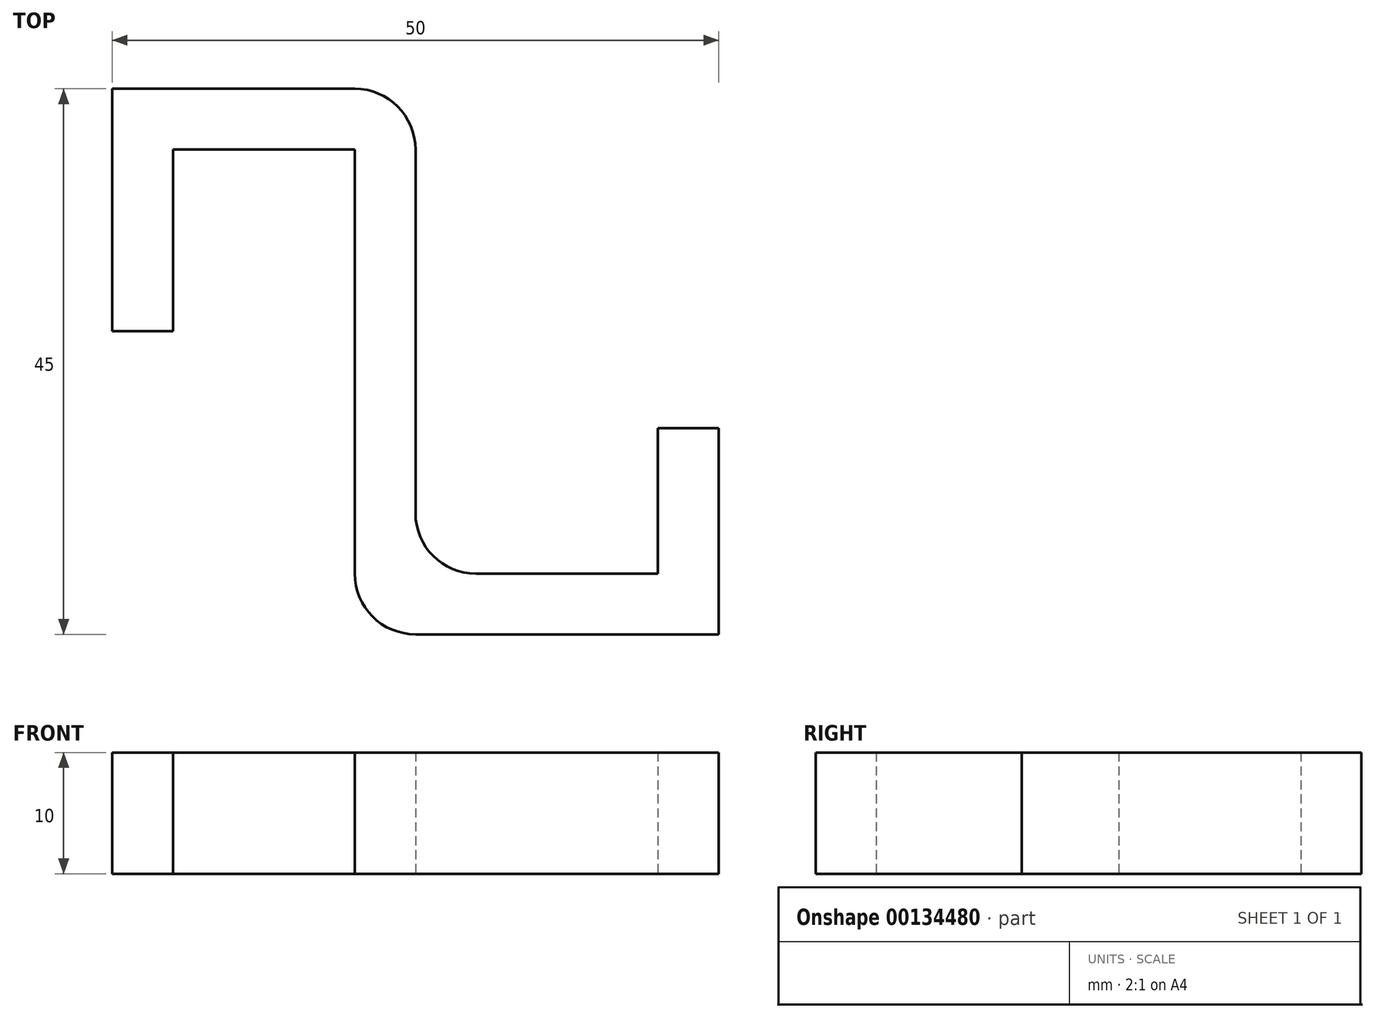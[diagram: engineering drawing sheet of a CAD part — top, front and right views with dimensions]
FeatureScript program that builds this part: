
annotation { "Feature Type Name" : "Feature", "Feature Type Description" : "" }
export const myFeature = defineFeature(function(context is Context, id is Id, definition is map)
    precondition{}
    {
        {
            var Q0;
            Q0=qCreatedBy(makeId("Top.planeOp"),FACE);
            var sketch = newSketch(context, id + "F0", { "sketchPlane" : qUnion([Q0])});
            skLineSegment(sketch, "E0", {"start": v(0, 0) * mm, "end": v(0, 15) * mm});
            skLineSegment(sketch, "E1", {"start": v(0, 15) * mm, "end": v(15, 15) * mm});
            skLineSegment(sketch, "E2", {"start": v(15, 15) * mm, "end": v(15, -25) * mm});
            skLineSegment(sketch, "E3", {"start": v(15, -25) * mm, "end": v(45, -25) * mm});
            skLineSegment(sketch, "E4", {"start": v(45, -25) * mm, "end": v(45, -8) * mm});
            skLineSegment(sketch, "E5", {"start": v(45, -8) * mm, "end": v(40, -8) * mm});
            skLineSegment(sketch, "E6", {"start": v(40, -8) * mm, "end": v(40, -20) * mm});
            skLineSegment(sketch, "E7", {"start": v(40, -20) * mm, "end": v(20, -20) * mm});
            skLineSegment(sketch, "E8", {"start": v(20, -20) * mm, "end": v(20, 20) * mm});
            skLineSegment(sketch, "E9", {"start": v(20, 20) * mm, "end": v(-5, 20) * mm});
            skLineSegment(sketch, "E10", {"start": v(-5, 20) * mm, "end": v(-5, 0) * mm});
            skLineSegment(sketch, "E11", {"start": v(-5, 0) * mm, "end": v(0, 0) * mm});
            skSolve(sketch);
        }
        {
            var Q0;
            Q0 = qSketchRegion(id + "F0", true);
            extrude(context, id + "F1", {"entities" : qUnion([Q0]), "depth" : 10 * mm});
        }
        {
            var Q0;
            Q0=makeQuery(id+"F1.opExtrude","SWEPT_EDGE",EDGE,{"disambiguationData":[OSD([sQuery(id+"F0.wireOp",EDGE,"E7"),sQuery(id+"F0.wireOp",EDGE,"E8")])]});
            var Q1;
            Q1=makeQuery(id+"F1.opExtrude","SWEPT_EDGE",EDGE,{"disambiguationData":[OSD([sQuery(id+"F0.wireOp",EDGE,"E8"),sQuery(id+"F0.wireOp",EDGE,"E9")])]});
            var Q2;
            Q2=makeQuery(id+"F1.opExtrude","SWEPT_EDGE",EDGE,{"disambiguationData":[OSD([sQuery(id+"F0.wireOp",EDGE,"E2"),sQuery(id+"F0.wireOp",EDGE,"E3")])]});
            fillet(context, id + "F2", {"entities" : qUnion([Q0, Q1, Q2]), "radius" : 5 * mm, "tangentPropagation" : true, "allowEdgeOverflow" : false});
        }
    });
